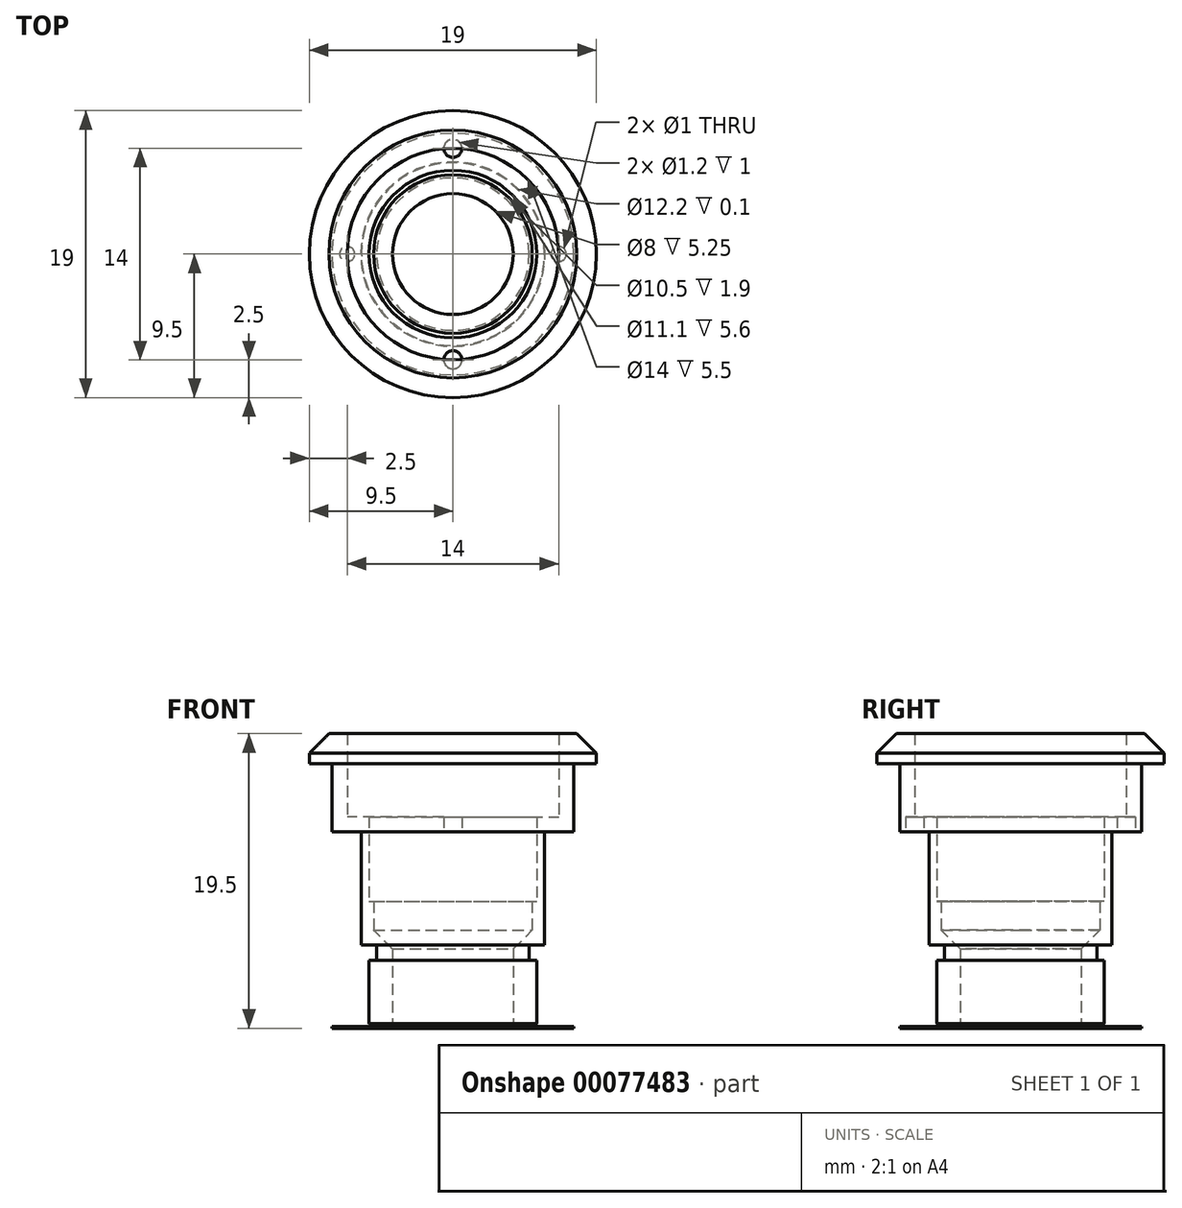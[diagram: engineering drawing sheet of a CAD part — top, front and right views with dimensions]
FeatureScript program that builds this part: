
annotation { "Feature Type Name" : "Feature", "Feature Type Description" : "" }
export const myFeature = defineFeature(function(context is Context, id is Id, definition is map)
    precondition{}
    {
        {
            var Q0;
            Q0=qCreatedBy(makeId("Front.planeOp"),FACE);
            var sketch = newSketch(context, id + "F0", { "sketchPlane" : qUnion([Q0])});
            skLineSegment(sketch, "E0", {"start": v(-4, 0) * mm, "end": v(-4, 5.25) * mm});
            skLineSegment(sketch, "E1", {"start": v(-4, 5.25) * mm, "end": v(-5.25, 6.5) * mm});
            skLineSegment(sketch, "E2", {"start": v(-5.25, 6.5) * mm, "end": v(-5.25, 8.4) * mm});
            skLineSegment(sketch, "E3", {"start": v(-5.25, 8.4) * mm, "end": v(-5.55, 8.4) * mm});
            skLineSegment(sketch, "E4", {"start": v(-5.55, 8.4) * mm, "end": v(-5.55, 14) * mm});
            skLineSegment(sketch, "E5", {"start": v(-5.55, 14) * mm, "end": v(-7, 14) * mm});
            skLineSegment(sketch, "E6", {"start": v(-7, 14) * mm, "end": v(-7, 19.5) * mm});
            skLineSegment(sketch, "E7", {"start": v(-7, 19.5) * mm, "end": v(-8.2, 19.5) * mm});
            skLineSegment(sketch, "E8", {"start": v(-8.2, 19.5) * mm, "end": v(-9.5, 18.2) * mm});
            skLineSegment(sketch, "E9", {"start": v(-9.5, 18.2) * mm, "end": v(-9.5, 17.5) * mm});
            skLineSegment(sketch, "E10", {"start": v(-9.5, 17.5) * mm, "end": v(-8, 17.5) * mm});
            skLineSegment(sketch, "E11", {"start": v(-8, 17.5) * mm, "end": v(-8, 13) * mm});
            skLineSegment(sketch, "E12", {"start": v(-8, 13) * mm, "end": v(-6.05, 13) * mm});
            skLineSegment(sketch, "E13", {"start": v(-6.05, 13) * mm, "end": v(-6.05, 5.5) * mm});
            skLineSegment(sketch, "E14", {"start": v(-6.05, 5.5) * mm, "end": v(-5.05, 5.5) * mm});
            skLineSegment(sketch, "E15", {"start": v(-5.05, 5.5) * mm, "end": v(-5.05, 4.5) * mm});
            skLineSegment(sketch, "E16", {"start": v(-5.05, 4.5) * mm, "end": v(-5.55, 4.5) * mm});
            skLineSegment(sketch, "E17", {"start": v(-5.55, 4.5) * mm, "end": v(-5.55, 0.3) * mm});
            skLineSegment(sketch, "E18", {"start": v(-5.55, 0.3) * mm, "end": v(-5.25, 0) * mm});
            skLineSegment(sketch, "E19", {"start": v(-5.25, 0) * mm, "end": v(-4, 0) * mm});
            skLineSegment(sketch, "E20", {"start": v(0, 0) * mm, "end": v(0, 19.5) * mm, "construction": true});
            skSolve(sketch);
        }
        {
            var Q0;
            Q0=makeQuery(id+"F0.imprint","IMPRINT",FACE,{"disambiguationData":[TD([[makeQuery(id+"F0.imprint","IMPRINT",EDGE,{"derivedFrom":sQuery(id+"F0.wireOp",EDGE,"E0")}),1.0]])]});
            var Q1;
            Q1=sQuery(id+"F0.wireOp",EDGE,"E20");
            revolve(context, id + "F1", {"entities" : qUnion([Q0]), "axis" : qUnion([Q1]), "revolveType" : RevolveType.FULL});
        }
        {
            var Q0;
            Q0=makeQuery(id+"F1.opRevolve","SWEPT_FACE",FACE,{"disambiguationData":[OSD([sQuery(id+"F0.wireOp",EDGE,"E12")])]});
            var sketch = newSketch(context, id + "F2", { "sketchPlane" : qUnion([Q0])});
            skCircle(sketch, "E21", {"center": v(0, 0) * mm, "radius": 7 * mm, "construction": true});
            skCircle(sketch, "E22", {"center": v(0, 7) * mm, "radius": 0.6 * mm});
            skCircle(sketch, "E23", {"center": v(0, -7) * mm, "radius": 0.6 * mm});
            skSolve(sketch);
        }
        {
            var Q0;
            {Q0=qUnion([makeQuery(id+"F2.imprint","IMPRINT",FACE,{"disambiguationData":[TD([[makeQuery(id+"F2.imprint","IMPRINT",EDGE,{"derivedFrom":sQuery(id+"F2.wireOp",EDGE,"E22")}),1.0]])]}),makeQuery(id+"F2.imprint","IMPRINT",FACE,{"disambiguationData":[TD([[makeQuery(id+"F2.imprint","IMPRINT",EDGE,{"derivedFrom":sQuery(id+"F2.wireOp",EDGE,"E23")}),1.0]])]})]);}
            extrude(context, id + "F3", {"entities" : qUnion([Q0]), "operationType" : NewBodyOperationType.REMOVE, "oppositeDirection" : true, "depth" : 1 * mm});
        }
        {
            var Q0;
            Q0=qCreatedBy(makeId("Top.planeOp"),FACE);
            var sketch = newSketch(context, id + "F4", { "sketchPlane" : qUnion([Q0])});
            skCircle(sketch, "E24", {"center": v(0, 0) * mm, "radius": 8 * mm});
            skCircle(sketch, "E25", {"center": v(0, 0) * mm, "radius": 6.1 * mm});
            skCircle(sketch, "E26", {"center": v(-7, 0) * mm, "radius": 0.5 * mm});
            skCircle(sketch, "E27", {"center": v(7, 0) * mm, "radius": 0.5 * mm});
            skSolve(sketch);
        }
        {
            var Q0;
            Q0=makeQuery(id+"F4.imprint","IMPRINT",FACE,{"disambiguationData":[TD([[makeQuery(id+"F4.imprint","IMPRINT",EDGE,{"derivedFrom":sQuery(id+"F4.wireOp",EDGE,"E24")}),1.0]])]});
            extrude(context, id + "F5", {"entities" : qUnion([Q0]), "depth" : 0.1 * mm});
        }
    });
